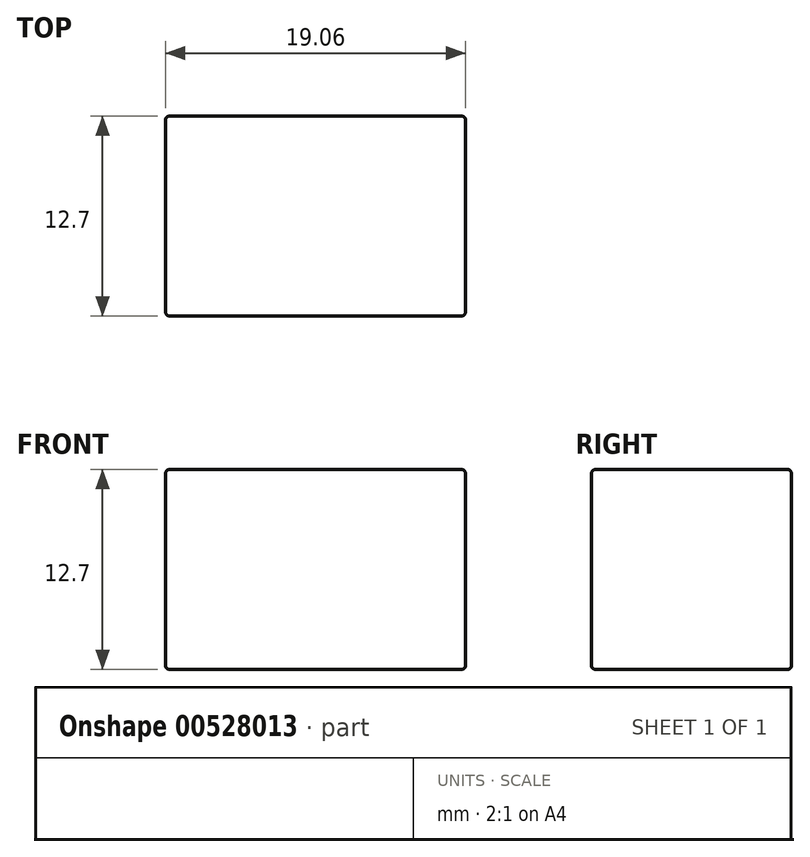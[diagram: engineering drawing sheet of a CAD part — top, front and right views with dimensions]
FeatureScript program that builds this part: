
annotation { "Feature Type Name" : "Feature", "Feature Type Description" : "" }
export const myFeature = defineFeature(function(context is Context, id is Id, definition is map)
    precondition{}
    {
        {
            var Q0;
            Q0=qCreatedBy(makeId("Front.planeOp"),FACE);
            var sketch = newSketch(context, id + "F0", { "sketchPlane" : qUnion([Q0])});
            skLineSegment(sketch, "E0.bottom", {"start": v(9.52, -6.35) * mm, "end": v(-9.53, -6.35) * mm});
            skLineSegment(sketch, "E0.top", {"start": v(9.53, 6.35) * mm, "end": v(-9.52, 6.35) * mm});
            skLineSegment(sketch, "E0.left", {"start": v(9.52, -6.35) * mm, "end": v(9.53, 6.35) * mm});
            skLineSegment(sketch, "E0.right", {"start": v(-9.53, -6.35) * mm, "end": v(-9.52, 6.35) * mm});
            skPoint(sketch, "E0.middle", {"position": v(0, 0) * mm});
            skSolve(sketch);
        }
        {
            var Q0;
            Q0 = qSketchRegion(id + "F0", true);
            extrude(context, id + "F1", {"entities" : qUnion([Q0]), "depth" : 12.7 * mm, "offsetDistance" : 25 * mm});
        }
        {
            var Q0;
            Q0=makeQuery(id+"F1.opExtrude","SWEPT_FACE",FACE,{"disambiguationData":[OSD([sQuery(id+"F0.wireOp",EDGE,"E0.top")])]});
            var Q1;
            Q1=makeQuery(id+"F1.opExtrude","CAP_FACE",FACE,{"disambiguationData":[OSD([sQuery(id+"F0.wireOp",EDGE,"E0.bottom"),sQuery(id+"F0.wireOp",EDGE,"E0.top"),sQuery(id+"F0.wireOp",EDGE,"E0.left"),sQuery(id+"F0.wireOp",EDGE,"E0.right")])],"isStart":false});
            var Q2;
            Q2=makeQuery(id+"F1.opExtrude","SWEPT_FACE",FACE,{"disambiguationData":[OSD([sQuery(id+"F0.wireOp",EDGE,"E0.left")])]});
            var Q3;
            Q3=makeQuery(id+"F1.opExtrude","SWEPT_FACE",FACE,{"disambiguationData":[OSD([sQuery(id+"F0.wireOp",EDGE,"E0.bottom")])]});
            var Q4;
            Q4=makeQuery(id+"F1.opExtrude","SWEPT_FACE",FACE,{"disambiguationData":[OSD([sQuery(id+"F0.wireOp",EDGE,"E0.right")])]});
            fillet(context, id + "F2", {"entities" : qUnion([Q0, Q1, Q2, Q3, Q4]), "radius" : .25 * mm, "tangentPropagation" : true, "allowEdgeOverflow" : false});
        }
    });
